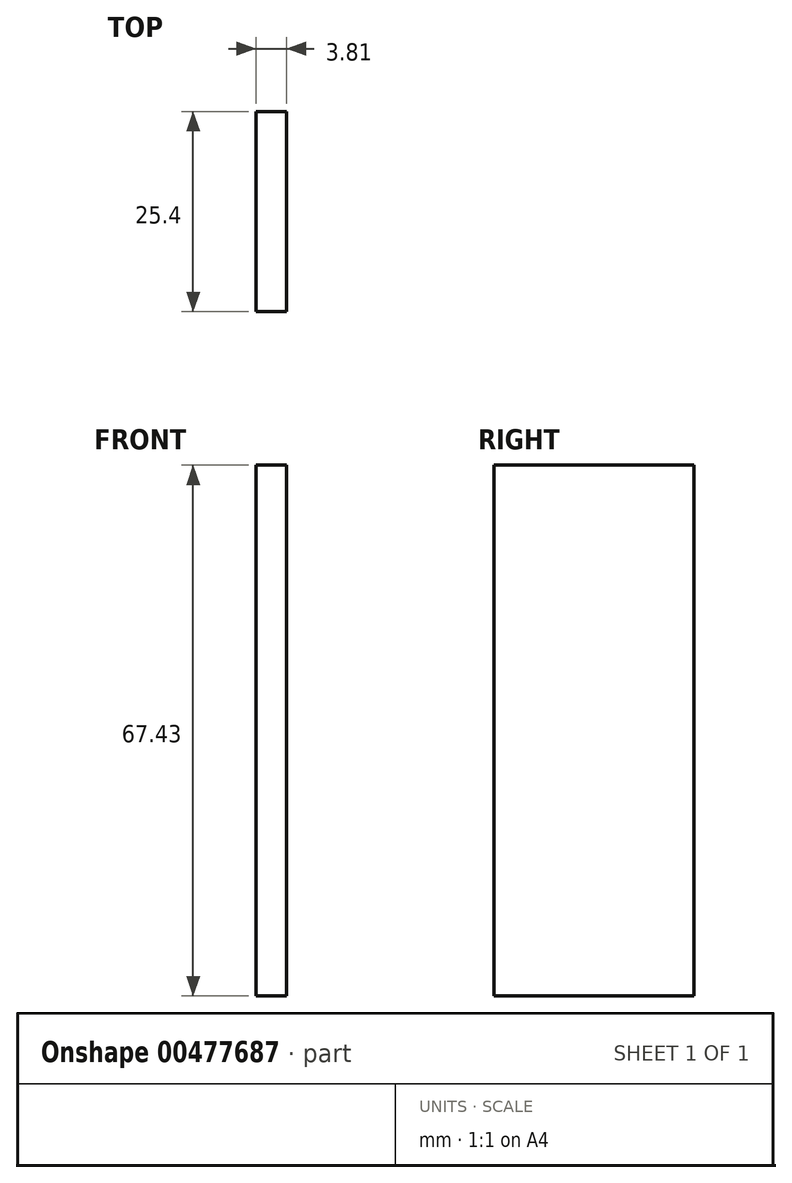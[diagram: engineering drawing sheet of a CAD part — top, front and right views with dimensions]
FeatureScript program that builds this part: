
annotation { "Feature Type Name" : "Feature", "Feature Type Description" : "" }
export const myFeature = defineFeature(function(context is Context, id is Id, definition is map)
    precondition{}
    {
        {
            var Q0;
            Q0=qCreatedBy(makeId("Front.planeOp"),FACE);
            var sketch = newSketch(context, id + "F0", { "sketchPlane" : qUnion([Q0])});
            skLineSegment(sketch, "E0.bottom", {"start": v(-52.3, 19.02) * mm, "end": v(-48.5, 19.02) * mm});
            skLineSegment(sketch, "E0.top", {"start": v(-52.3, 86.45) * mm, "end": v(-48.5, 86.45) * mm});
            skLineSegment(sketch, "E0.left", {"start": v(-52.3, 19.02) * mm, "end": v(-52.3, 86.45) * mm});
            skLineSegment(sketch, "E0.right", {"start": v(-48.5, 19.02) * mm, "end": v(-48.5, 86.45) * mm});
            skSolve(sketch);
        }
        {
            var Q0;
            Q0 = qSketchRegion(id + "F0", true);
            extrude(context, id + "F1", {"entities" : qUnion([Q0]), "depth" : 25.4 * mm});
        }
    });
